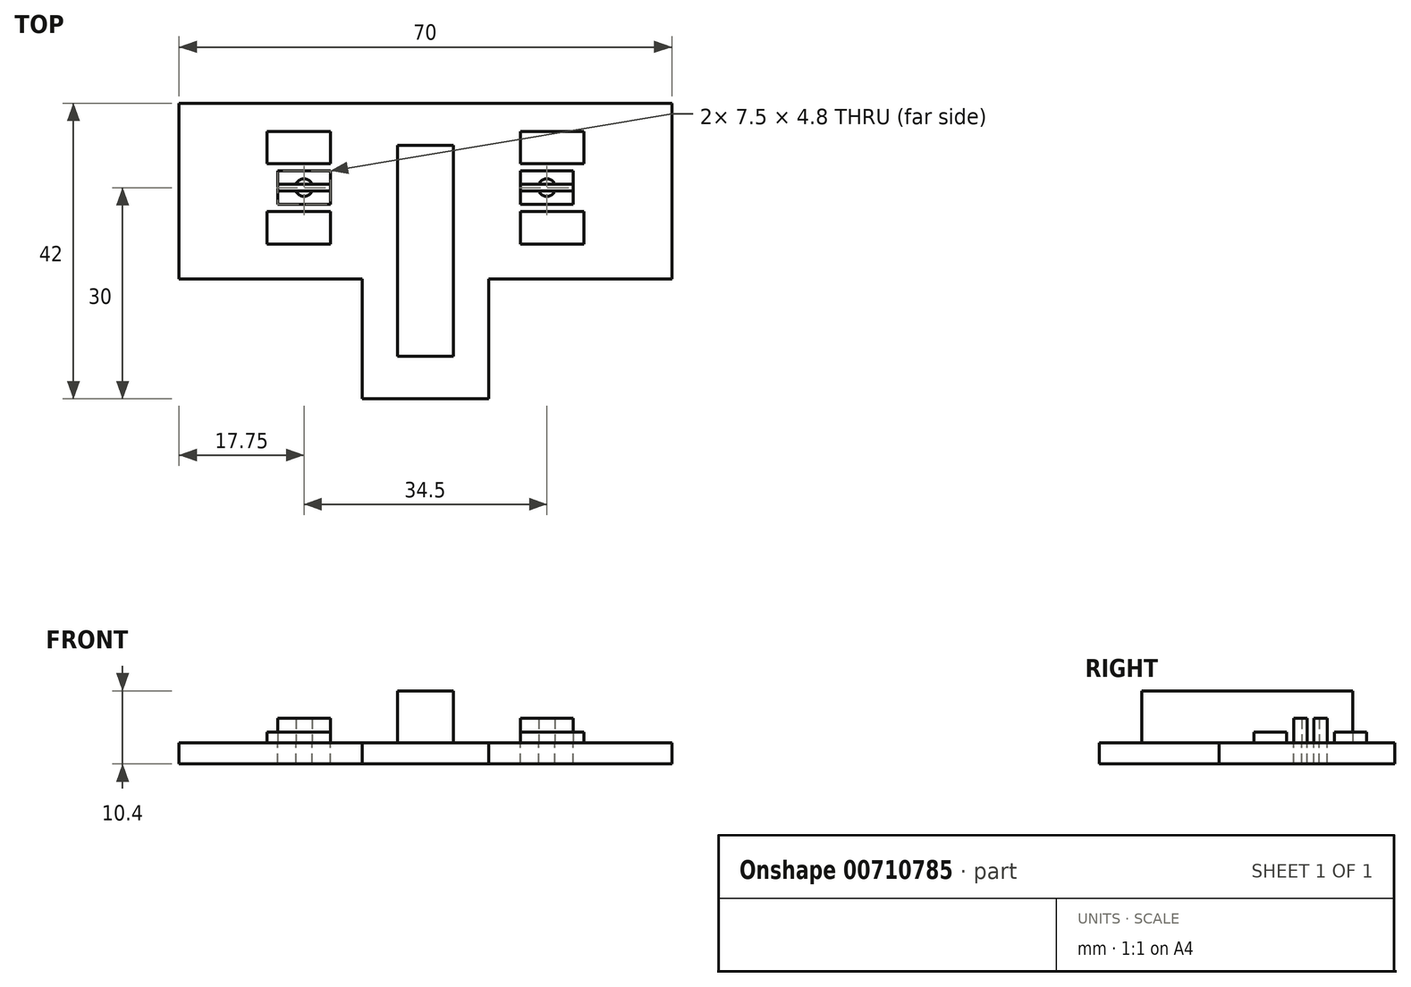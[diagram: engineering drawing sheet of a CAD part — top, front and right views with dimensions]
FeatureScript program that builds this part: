
annotation { "Feature Type Name" : "Feature", "Feature Type Description" : "" }
export const myFeature = defineFeature(function(context is Context, id is Id, definition is map)
    precondition{}
    {
        {
            var Q0;
            Q0=qCreatedBy(makeId("Front.planeOp"),FACE);
            var sketch = newSketch(context, id + "F0", { "sketchPlane" : qUnion([Q0])});
            skLineSegment(sketch, "E0", {"start": v(0, 0) * mm, "end": v(0, 78.64) * mm, "construction": true});
            skLineSegment(sketch, "E1", {"start": v(35, 0) * mm, "end": v(-35, 0) * mm});
            skLineSegment(sketch, "E2", {"start": v(-35, 3) * mm, "end": v(-3.95, 3) * mm});
            skLineSegment(sketch, "E3", {"start": v(-3.95, 3) * mm, "end": v(-3.95, 10.4) * mm});
            skLineSegment(sketch, "E4", {"start": v(-3.95, 10.4) * mm, "end": v(0, 10.4) * mm});
            skLineSegment(sketch, "E5", {"start": v(-35, 0) * mm, "end": v(-35, 3) * mm});
            skLineSegment(sketch, "E6.MirrorCS", {"start": v(35, 0) * mm, "end": v(35, 3) * mm});
            skLineSegment(sketch, "E7.MirrorCS", {"start": v(3.95, 10.4) * mm, "end": v(0, 10.4) * mm});
            skLineSegment(sketch, "E8.MirrorCS", {"start": v(35, 3) * mm, "end": v(3.95, 3) * mm});
            skLineSegment(sketch, "E9.MirrorCS", {"start": v(3.95, 3) * mm, "end": v(3.95, 10.4) * mm});
            skSolve(sketch);
        }
        {
            var Q0;
            Q0=makeQuery(id+"F0.imprint","IMPRINT",FACE,{"disambiguationData":[TD([[makeQuery(id+"F0.imprint","IMPRINT",EDGE,{"derivedFrom":sQuery(id+"F0.wireOp",EDGE,"E1")}),-1.0]])]});
            extrude(context, id + "F1", {"entities" : qUnion([Q0]), "endBound" : BoundingType.SYMMETRIC, "depth" : 42 * mm, "offsetDistance" : 25 * mm});
        }
        {
            var Q0;
            Q0=makeQuery(id+"F1.opExtrude","SWEPT_FACE",FACE,{"disambiguationData":[OSD([sQuery(id+"F0.wireOp",EDGE,"E1")])]});
            var sketch = newSketch(context, id + "F2", { "sketchPlane" : qUnion([Q0])});
            skLineSegment(sketch, "E10", {"start": v(0, 28.89) * mm, "end": v(0, -29.28) * mm, "construction": true});
            skLineSegment(sketch, "E11", {"start": v(-9, 21) * mm, "end": v(9, 21) * mm, "construction": true});
            skPoint(sketch, "E12", {"position": v(0, 21) * mm});
            skLineSegment(sketch, "E13.bottom", {"start": v(35, 21) * mm, "end": v(9, 21) * mm});
            skLineSegment(sketch, "E13.top", {"start": v(35, 4) * mm, "end": v(9, 4) * mm});
            skLineSegment(sketch, "E13.left", {"start": v(35, 21) * mm, "end": v(35, 4) * mm});
            skLineSegment(sketch, "E13.right", {"start": v(9, 21) * mm, "end": v(9, 4) * mm});
            skLineSegment(sketch, "E14.MirrorCS", {"start": v(-35, 21) * mm, "end": v(-35, 4) * mm});
            skLineSegment(sketch, "E15.MirrorCS", {"start": v(9, 21) * mm, "end": v(-9, 21) * mm, "construction": true});
            skLineSegment(sketch, "E16.MirrorCS", {"start": v(-35, 4) * mm, "end": v(-9, 4) * mm});
            skLineSegment(sketch, "E17.MirrorCS", {"start": v(-35, 21) * mm, "end": v(-9, 21) * mm});
            skLineSegment(sketch, "E18.MirrorCS", {"start": v(-9, 21) * mm, "end": v(-9, 4) * mm});
            skSolve(sketch);
        }
        {
            var Q0;
            Q0=makeQuery(id+"F2.imprint","IMPRINT",FACE,{"disambiguationData":[TD([[makeQuery(id+"F2.imprint","IMPRINT",EDGE,{"derivedFrom":sQuery(id+"F2.wireOp",EDGE,"E14.MirrorCS")}),1.0]])]});
            var Q1;
            Q1=makeQuery(id+"F2.imprint","IMPRINT",FACE,{"disambiguationData":[TD([[makeQuery(id+"F2.imprint","IMPRINT",EDGE,{"derivedFrom":sQuery(id+"F2.wireOp",EDGE,"E13.bottom")}),1.0]])]});
            extrude(context, id + "F3", {"entities" : qUnion([Q0, Q1]), "operationType" : NewBodyOperationType.REMOVE, "oppositeDirection" : true, "depth" : 25 * mm, "offsetDistance" : 25 * mm});
        }
        {
            var Q0;
            Q0=makeQuery(id+"F1.opExtrude","SWEPT_FACE",FACE,{"disambiguationData":[OSD([sQuery(id+"F0.wireOp",EDGE,"E3")])]});
            var sketch = newSketch(context, id + "F4", { "sketchPlane" : qUnion([Q0])});
            skLineSegment(sketch, "E19.bottom", {"start": v(21, 10.4) * mm, "end": v(15, 10.4) * mm});
            skLineSegment(sketch, "E19.top", {"start": v(21, 3) * mm, "end": v(15, 3) * mm});
            skLineSegment(sketch, "E19.left", {"start": v(21, 10.4) * mm, "end": v(21, 3) * mm});
            skLineSegment(sketch, "E19.right", {"start": v(15, 10.4) * mm, "end": v(15, 3) * mm});
            skLineSegment(sketch, "E20", {"start": v(0, 12.19) * mm, "end": v(0, 0) * mm, "construction": true});
            skLineSegment(sketch, "E21.MirrorCS", {"start": v(-21, 10.4) * mm, "end": v(-15, 10.4) * mm});
            skLineSegment(sketch, "E22.MirrorCS", {"start": v(-15, 10.4) * mm, "end": v(-15, 3) * mm});
            skLineSegment(sketch, "E23.MirrorCS", {"start": v(-21, 10.4) * mm, "end": v(-21, 3) * mm});
            skLineSegment(sketch, "E24.MirrorCS", {"start": v(-21, 3) * mm, "end": v(-15, 3) * mm});
            skSolve(sketch);
        }
        {
            var Q0;
            Q0=makeQuery(id+"F4.imprint","IMPRINT",FACE,{"disambiguationData":[TD([[makeQuery(id+"F4.imprint","IMPRINT",EDGE,{"derivedFrom":sQuery(id+"F4.wireOp",EDGE,"E21.MirrorCS")}),1.0]])]});
            var Q1;
            Q1=makeQuery(id+"F4.imprint","IMPRINT",FACE,{"disambiguationData":[TD([[makeQuery(id+"F4.imprint","IMPRINT",EDGE,{"derivedFrom":sQuery(id+"F4.wireOp",EDGE,"E19.bottom")}),1.0]])]});
            extrude(context, id + "F5", {"entities" : qUnion([Q0, Q1]), "operationType" : NewBodyOperationType.REMOVE, "oppositeDirection" : true, "depth" : 25 * mm, "offsetDistance" : 25 * mm});
        }
        {
            var Q0;
            Q0=makeQuery(id+"F5.boolean.opBoolean","MERGE",FACE,{"derivedFrom":[makeQuery(id+"F1.opExtrude","SWEPT_FACE",FACE,{"disambiguationData":[OSD([sQuery(id+"F0.wireOp",EDGE,"E2")])]}),makeQuery(id+"F1.opExtrude","SWEPT_FACE",FACE,{"disambiguationData":[OSD([sQuery(id+"F0.wireOp",EDGE,"E8.MirrorCS")])]}),makeQuery(id+"F5.opExtrude","SWEPT_FACE",FACE,{"disambiguationData":[OSD([sQuery(id+"F4.wireOp",EDGE,"E19.top")])]}),makeQuery(id+"F5.opExtrude","SWEPT_FACE",FACE,{"disambiguationData":[OSD([sQuery(id+"F4.wireOp",EDGE,"E24.MirrorCS")])]})]});
            var sketch = newSketch(context, id + "F6", { "sketchPlane" : qUnion([Q0])});
            skLineSegment(sketch, "E25", {"start": v(0, 15.74) * mm, "end": v(0, -14.12) * mm, "construction": true});
            skLineSegment(sketch, "E26", {"start": v(-22.5, 9) * mm, "end": v(22.5, 9) * mm, "construction": true});
            skPoint(sketch, "E27", {"position": v(0, 9) * mm});
            skLineSegment(sketch, "E28.bottom", {"start": v(22.5, 17) * mm, "end": v(13.5, 17) * mm});
            skLineSegment(sketch, "E28.top", {"start": v(22.5, 1) * mm, "end": v(13.5, 1) * mm});
            skLineSegment(sketch, "E28.left", {"start": v(22.5, 17) * mm, "end": v(22.5, 1) * mm});
            skLineSegment(sketch, "E28.right", {"start": v(13.5, 17) * mm, "end": v(13.5, 1) * mm});
            skLineSegment(sketch, "E29.bottom", {"start": v(13.5, 11.4) * mm, "end": v(21, 11.4) * mm});
            skLineSegment(sketch, "E29.top", {"start": v(13.5, 6.6) * mm, "end": v(21, 6.6) * mm});
            skLineSegment(sketch, "E29.left", {"start": v(13.5, 11.4) * mm, "end": v(13.5, 6.6) * mm});
            skLineSegment(sketch, "E29.right", {"start": v(21, 11.4) * mm, "end": v(21, 6.6) * mm});
            skPoint(sketch, "E30", {"position": v(13.5, 9) * mm});
            skLineSegment(sketch, "E31", {"start": v(13.5, 12.4) * mm, "end": v(22.5, 12.4) * mm});
            skLineSegment(sketch, "E32", {"start": v(13.5, 5.6) * mm, "end": v(22.5, 5.6) * mm});
            skLineSegment(sketch, "E33.bottom", {"start": v(13.5, 9.5) * mm, "end": v(21, 9.5) * mm});
            skLineSegment(sketch, "E33.top", {"start": v(13.5, 8.5) * mm, "end": v(21, 8.5) * mm});
            skLineSegment(sketch, "E33.left", {"start": v(13.5, 9.5) * mm, "end": v(13.5, 8.5) * mm});
            skLineSegment(sketch, "E33.right", {"start": v(21, 9.5) * mm, "end": v(21, 8.5) * mm});
            skLineSegment(sketch, "E34.MirrorCS", {"start": v(-13.5, 11.4) * mm, "end": v(-13.5, 6.6) * mm});
            skLineSegment(sketch, "E35.MirrorCS", {"start": v(-13.5, 9.5) * mm, "end": v(-13.5, 8.5) * mm});
            skLineSegment(sketch, "E36.MirrorCS", {"start": v(-21, 11.4) * mm, "end": v(-21, 6.6) * mm});
            skLineSegment(sketch, "E37.MirrorCS", {"start": v(-13.5, 12.4) * mm, "end": v(-22.5, 12.4) * mm});
            skLineSegment(sketch, "E38.MirrorCS", {"start": v(-13.5, 5.6) * mm, "end": v(-22.5, 5.6) * mm});
            skLineSegment(sketch, "E39.MirrorCS", {"start": v(-13.5, 9.5) * mm, "end": v(-21, 9.5) * mm});
            skLineSegment(sketch, "E40.MirrorCS", {"start": v(-13.5, 6.6) * mm, "end": v(-21, 6.6) * mm});
            skLineSegment(sketch, "E41.MirrorCS", {"start": v(-13.5, 11.4) * mm, "end": v(-21, 11.4) * mm});
            skLineSegment(sketch, "E42.MirrorCS", {"start": v(-13.5, 17) * mm, "end": v(-13.5, 1) * mm});
            skLineSegment(sketch, "E43.MirrorCS", {"start": v(-22.5, 17) * mm, "end": v(-22.5, 1) * mm});
            skLineSegment(sketch, "E44.MirrorCS", {"start": v(-22.5, 1) * mm, "end": v(-13.5, 1) * mm});
            skLineSegment(sketch, "E45.MirrorCS", {"start": v(-22.5, 17) * mm, "end": v(-13.5, 17) * mm});
            skPoint(sketch, "E46.MirrorP", {"position": v(-13.5, 9) * mm});
            skLineSegment(sketch, "E47.MirrorCS", {"start": v(22.5, 9) * mm, "end": v(-22.5, 9) * mm, "construction": true});
            skLineSegment(sketch, "E48.MirrorCS", {"start": v(-13.5, 8.5) * mm, "end": v(-21, 8.5) * mm});
            skLineSegment(sketch, "E49.MirrorCS", {"start": v(-21, 9.5) * mm, "end": v(-21, 8.5) * mm});
            skPoint(sketch, "E50", {"position": v(21, 9) * mm});
            skPoint(sketch, "E51", {"position": v(17.25, 9) * mm});
            skLineSegment(sketch, "E52", {"start": v(13.5, 9) * mm, "end": v(21, 9) * mm, "construction": true});
            skCircle(sketch, "E53", {"center": v(17.25, 9) * mm, "radius": 1.25 * mm});
            skPoint(sketch, "E54.MirrorP", {"position": v(-17.25, 9) * mm});
            skCircle(sketch, "E55.MirrorC", {"center": v(-17.25, 9) * mm, "radius": 1.25 * mm});
            skSolve(sketch);
        }
        {
            var Q0;
            {var subQ0=sQuery(id+"F6.wireOp",EDGE,"E37.MirrorCS");Q0=makeQuery(id+"F6.imprint","IMPRINT",FACE,{"disambiguationData":[TD([[makeQuery(id+"F6.imprint","IMPRINT",EDGE,{"derivedFrom":subQ0}),-1.0]])]});}
            var Q1;
            {var subQ0=sQuery(id+"F6.wireOp",EDGE,"E38.MirrorCS");Q1=makeQuery(id+"F6.imprint","IMPRINT",FACE,{"disambiguationData":[TD([[makeQuery(id+"F6.imprint","IMPRINT",EDGE,{"derivedFrom":subQ0}),1.0]])]});}
            var Q2;
            {var subQ0=sQuery(id+"F6.wireOp",EDGE,"E28.bottom");Q2=makeQuery(id+"F6.imprint","IMPRINT",FACE,{"disambiguationData":[TD([[makeQuery(id+"F6.imprint","IMPRINT",EDGE,{"derivedFrom":subQ0}),1.0]])]});}
            var Q3;
            {var subQ0=sQuery(id+"F6.wireOp",EDGE,"E28.top");Q3=makeQuery(id+"F6.imprint","IMPRINT",FACE,{"disambiguationData":[TD([[makeQuery(id+"F6.imprint","IMPRINT",EDGE,{"derivedFrom":subQ0}),-1.0]])]});}
            extrude(context, id + "F7", {"entities" : qUnion([Q0, Q1, Q2, Q3]), "operationType" : NewBodyOperationType.ADD, "depth" : 1.5 * mm, "offsetDistance" : 25 * mm});
        }
        {
            var Q0;
            {var subQ2=sQuery(id+"F6.wireOp",EDGE,"E39.MirrorCS");Q0=makeQuery(id+"F6.imprint","IMPRINT",FACE,{"disambiguationData":[TD([[makeQuery(id+"F6.imprint","IMPRINT",EDGE,{"derivedFrom":subQ2}),-1.0]])]});}
            var Q1;
            {var subQ0=sQuery(id+"F6.wireOp",EDGE,"E40.MirrorCS");Q1=makeQuery(id+"F6.imprint","IMPRINT",FACE,{"disambiguationData":[TD([[makeQuery(id+"F6.imprint","IMPRINT",EDGE,{"derivedFrom":subQ0}),-1.0]])]});}
            var Q2;
            {var subQ0=sQuery(id+"F6.wireOp",EDGE,"E29.bottom");Q2=makeQuery(id+"F6.imprint","IMPRINT",FACE,{"disambiguationData":[TD([[makeQuery(id+"F6.imprint","IMPRINT",EDGE,{"derivedFrom":subQ0}),-1.0]])]});}
            var Q3;
            {var subQ0=sQuery(id+"F6.wireOp",EDGE,"E29.top");Q3=makeQuery(id+"F6.imprint","IMPRINT",FACE,{"disambiguationData":[TD([[makeQuery(id+"F6.imprint","IMPRINT",EDGE,{"derivedFrom":subQ0}),1.0]])]});}
            extrude(context, id + "F8", {"entities" : qUnion([Q0, Q1, Q2, Q3]), "operationType" : NewBodyOperationType.ADD, "depth" : 3.5 * mm, "offsetDistance" : 25 * mm});
        }
        {
            var Q0;
            {var subQ0=sQuery(id+"F6.wireOp",EDGE,"E39.MirrorCS");Q0=makeQuery(id+"F6.imprint","IMPRINT",FACE,{"disambiguationData":[TD([[makeQuery(id+"F6.imprint","IMPRINT",EDGE,{"derivedFrom":subQ0}),1.0]])]});}
            var Q1;
            Q1=makeQuery(id+"F6.imprint","IMPRINT",FACE,{"disambiguationData":[TD([[makeQuery(id+"F6.imprint","IMPRINT",EDGE,{"derivedFrom":sQuery(id+"F6.wireOp",EDGE,"E33.bottom")}),-1.0]])]});
            var Q2;
            {var subQ0=sQuery(id+"F6.wireOp",EDGE,"E55.MirrorC");var subQ1=sQuery(id+"F6.wireOp",EDGE,"E39.MirrorCS");var subQ2=makeQuery(id+"F6.imprint","INTERSECT",VERTEX,{"disambiguationData":[OD(0.0)],"derivedFrom":[subQ1,subQ0]});Q2=makeQuery(id+"F6.imprint","IMPRINT",FACE,{"disambiguationData":[TD([[makeQuery(id+"F6.imprint","IMPRINT",EDGE,{"disambiguationData":[TD([[subQ2,-1.0]])],"derivedFrom":subQ1}),-1.0]])]});}
            var Q3;
            {var subQ0=sQuery(id+"F6.wireOp",EDGE,"E55.MirrorC");var subQ1=sQuery(id+"F6.wireOp",EDGE,"E48.MirrorCS");var subQ2=makeQuery(id+"F6.imprint","INTERSECT",VERTEX,{"disambiguationData":[OD(0.0)],"derivedFrom":[subQ1,subQ0]});Q3=makeQuery(id+"F6.imprint","IMPRINT",FACE,{"disambiguationData":[TD([[makeQuery(id+"F6.imprint","IMPRINT",EDGE,{"disambiguationData":[TD([[subQ2,-1.0]])],"derivedFrom":subQ1}),1.0]])]});}
            var Q4;
            {var subQ0=sQuery(id+"F6.wireOp",EDGE,"E53");var subQ1=sQuery(id+"F6.wireOp",EDGE,"E33.bottom");var subQ2=makeQuery(id+"F6.imprint","INTERSECT",VERTEX,{"disambiguationData":[OD(0.0)],"derivedFrom":[subQ1,subQ0]});Q4=makeQuery(id+"F6.imprint","IMPRINT",FACE,{"disambiguationData":[TD([[makeQuery(id+"F6.imprint","IMPRINT",EDGE,{"disambiguationData":[TD([[subQ2,-1.0]])],"derivedFrom":subQ1}),1.0]])]});}
            var Q5;
            {var subQ0=sQuery(id+"F6.wireOp",EDGE,"E53");var subQ1=sQuery(id+"F6.wireOp",EDGE,"E33.top");var subQ2=makeQuery(id+"F6.imprint","INTERSECT",VERTEX,{"disambiguationData":[OD(0.0)],"derivedFrom":[subQ1,subQ0]});Q5=makeQuery(id+"F6.imprint","IMPRINT",FACE,{"disambiguationData":[TD([[makeQuery(id+"F6.imprint","IMPRINT",EDGE,{"disambiguationData":[TD([[subQ2,-1.0]])],"derivedFrom":subQ1}),-1.0]])]});}
            extrude(context, id + "F9", {"entities" : qUnion([Q0, Q1, Q2, Q3, Q4, Q5]), "operationType" : NewBodyOperationType.REMOVE, "endBound" : BoundingType.THROUGH_ALL, "oppositeDirection" : true, "depth" : 25 * mm, "offsetDistance" : 25 * mm});
        }
    });
